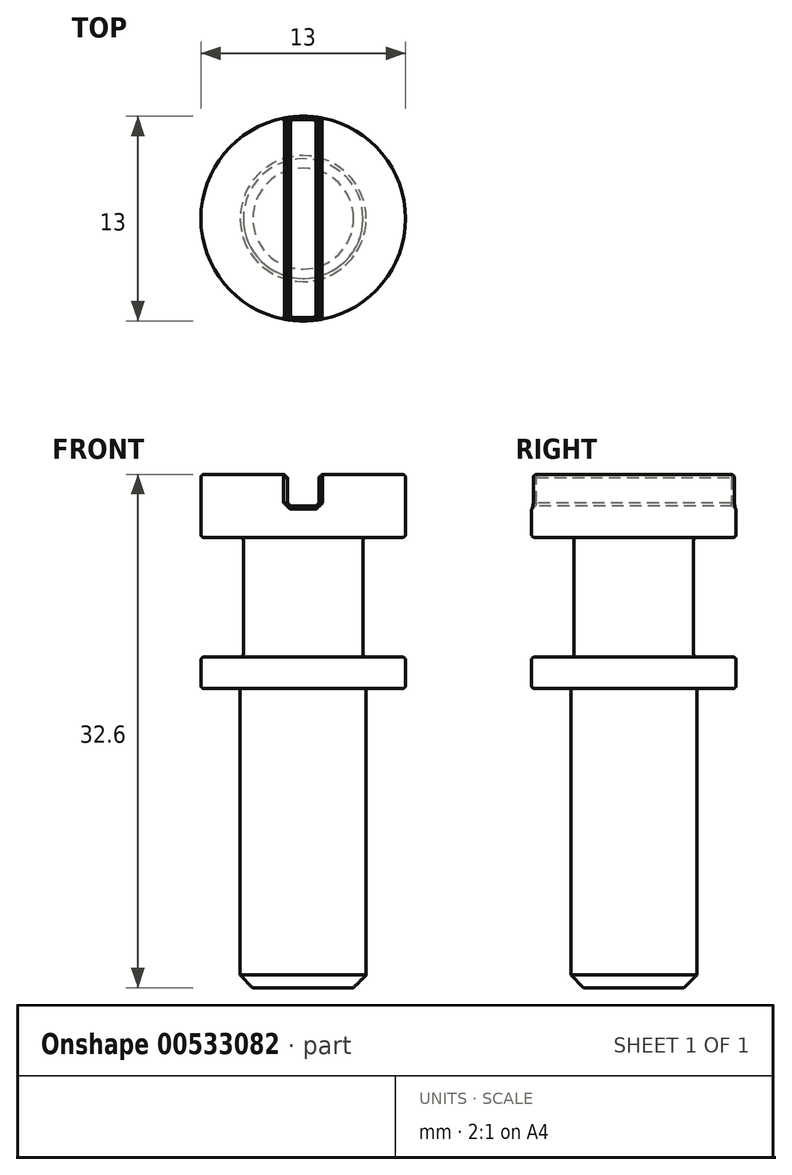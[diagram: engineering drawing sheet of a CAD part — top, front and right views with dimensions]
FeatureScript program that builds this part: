
annotation { "Feature Type Name" : "Feature", "Feature Type Description" : "" }
export const myFeature = defineFeature(function(context is Context, id is Id, definition is map)
    precondition{}
    {
        {
            var Q0;
            Q0=qCreatedBy(makeId("Front.planeOp"),FACE);
            var sketch = newSketch(context, id + "F0", { "sketchPlane" : qUnion([Q0])});
            skLineSegment(sketch, "E0", {"start": v(0, 4) * mm, "end": v(6.5, 4) * mm});
            skLineSegment(sketch, "E1", {"start": v(6.5, 4) * mm, "end": v(6.5, 0) * mm});
            skLineSegment(sketch, "E2", {"start": v(6.5, 0) * mm, "end": v(3.8, 0) * mm});
            skLineSegment(sketch, "E3", {"start": v(3.8, 0) * mm, "end": v(3.8, -7.6) * mm});
            skLineSegment(sketch, "E4", {"start": v(3.8, -7.6) * mm, "end": v(6.5, -7.6) * mm});
            skLineSegment(sketch, "E5", {"start": v(6.5, -9.6) * mm, "end": v(4, -9.6) * mm});
            skLineSegment(sketch, "E6", {"start": v(4, -28.6) * mm, "end": v(0, -28.6) * mm});
            skLineSegment(sketch, "E7", {"start": v(0, -28.6) * mm, "end": v(0, 4) * mm});
            skLineSegment(sketch, "E8", {"start": v(4, -9.6) * mm, "end": v(4, -28.6) * mm});
            skLineSegment(sketch, "E9", {"start": v(0, 4) * mm, "end": v(0, 10.35) * mm, "construction": true});
            skLineSegment(sketch, "E10", {"start": v(6.5, -7.6) * mm, "end": v(6.5, -9.6) * mm});
            skSolve(sketch);
        }
        {
            var Q0;
            Q0 = qSketchRegion(id + "F0", true);
            var Q1;
            Q1=sQuery(id+"F0.wireOp",EDGE,"E9");
            revolve(context, id + "F1", {"entities" : qUnion([Q0]), "axis" : qUnion([Q1]), "revolveType" : RevolveType.FULL});
        }
        {
            var Q0;
            Q0=qCreatedBy(makeId("Front.planeOp"),FACE);
            var sketch = newSketch(context, id + "F2", { "sketchPlane" : qUnion([Q0])});
            skLineSegment(sketch, "E11.bottom", {"start": v(1, 4) * mm, "end": v(-1, 4) * mm});
            skLineSegment(sketch, "E11.top", {"start": v(1, 2) * mm, "end": v(-1, 2) * mm});
            skLineSegment(sketch, "E11.left", {"start": v(1, 4) * mm, "end": v(1, 2) * mm});
            skLineSegment(sketch, "E11.right", {"start": v(-1, 4) * mm, "end": v(-1, 2) * mm});
            skPoint(sketch, "E11.middle", {"position": v(0, 3) * mm});
            skSolve(sketch);
        }
        {
            var Q0;
            Q0 = qSketchRegion(id + "F2", true);
            extrude(context, id + "F3", {"entities" : qUnion([Q0]), "operationType" : NewBodyOperationType.REMOVE, "endBound" : BoundingType.THROUGH_ALL, "oppositeDirection" : true, "depth" : 25 * mm, "offsetDistance" : 25 * mm, "hasSecondDirection" : true, "secondDirectionBound" : SecondDirectionBoundingType.THROUGH_ALL, "secondDirectionOppositeDirection" : false, "secondDirectionDepth" : 25 * mm});
        }
        {
            var Q0;
            {var subQ0=sQuery(id+"F0.wireOp",EDGE,"E0");var subQ1=sQuery(id+"F0.wireOp",EDGE,"E1");Q0=makeQuery(id+"F3.boolean.opBoolean","SPLIT",EDGE,{"disambiguationData":[TD([makeQuery(id+"F3.opExtrude","SWEPT_FACE",FACE,{"disambiguationData":[OSD([sQuery(id+"F2.wireOp",EDGE,"E11.right")])]})])],"derivedFrom":makeQuery(id+"F1.opRevolve","SWEPT_EDGE",EDGE,{"disambiguationData":[OSD([subQ0,subQ1])]})});}
            var Q1;
            {var subQ0=sQuery(id+"F0.wireOp",EDGE,"E0");var subQ1=sQuery(id+"F0.wireOp",EDGE,"E1");Q1=makeQuery(id+"F3.boolean.opBoolean","SPLIT",EDGE,{"disambiguationData":[TD([makeQuery(id+"F3.opExtrude","SWEPT_FACE",FACE,{"disambiguationData":[OSD([sQuery(id+"F2.wireOp",EDGE,"E11.left")])]})])],"derivedFrom":makeQuery(id+"F1.opRevolve","SWEPT_EDGE",EDGE,{"disambiguationData":[OSD([subQ0,subQ1])]})});}
            var Q2;
            Q2=makeQuery(id+"F1.opRevolve","SWEPT_FACE",FACE,{"disambiguationData":[OSD([sQuery(id+"F0.wireOp",EDGE,"E2")])]});
            var Q3;
            Q3=makeQuery(id+"F1.opRevolve","SWEPT_FACE",FACE,{"disambiguationData":[OSD([sQuery(id+"F0.wireOp",EDGE,"E4")])]});
            var Q4;
            Q4=makeQuery(id+"F1.opRevolve","SWEPT_EDGE",EDGE,{"disambiguationData":[OSD([sQuery(id+"F0.wireOp",EDGE,"E5"),sQuery(id+"F0.wireOp",EDGE,"E10")])]});
            fillet(context, id + "F4", {"entities" : qUnion([Q0, Q1, Q2, Q3, Q4]), "radius" : .2 * mm, "tangentPropagation" : true, "allowEdgeOverflow" : false});
        }
        {
            var Q0;
            Q0=makeQuery(id+"F3.boolean.opBoolean","COPY",FACE,{"derivedFrom":makeQuery(id+"F3.opExtrude","SWEPT_FACE",FACE,{"disambiguationData":[OSD([sQuery(id+"F2.wireOp",EDGE,"E11.right")])]})});
            var Q1;
            Q1=makeQuery(id+"F3.boolean.opBoolean","COPY",FACE,{"derivedFrom":makeQuery(id+"F3.opExtrude","SWEPT_FACE",FACE,{"disambiguationData":[OSD([sQuery(id+"F2.wireOp",EDGE,"E11.left")])]})});
            chamfer(context, id + "F5", {"entities" : qUnion([Q0, Q1]), "width" : .2 * mm, "tangentPropagation" : true});
        }
        {
            var Q0;
            Q0=makeQuery(id+"F1.opRevolve","SWEPT_EDGE",EDGE,{"disambiguationData":[OSD([sQuery(id+"F0.wireOp",EDGE,"E6"),sQuery(id+"F0.wireOp",EDGE,"E8")])]});
            chamfer(context, id + "F6", {"entities" : qUnion([Q0]), "width" : .8 * mm, "tangentPropagation" : true});
        }
    });
